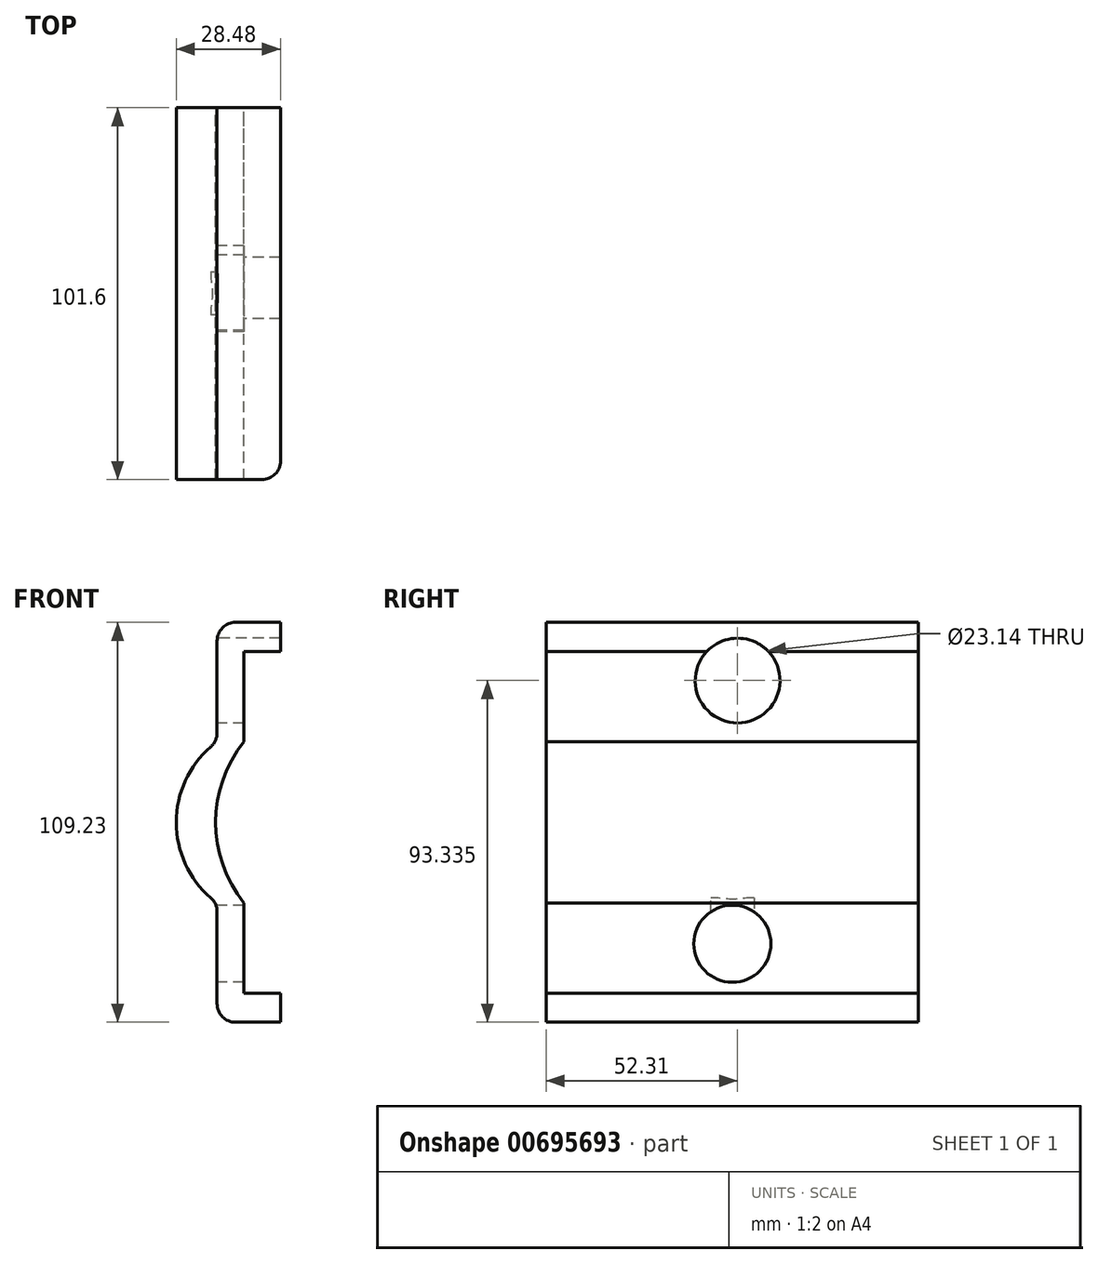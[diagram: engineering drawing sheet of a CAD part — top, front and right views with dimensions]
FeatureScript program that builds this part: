
annotation { "Feature Type Name" : "Feature", "Feature Type Description" : "" }
export const myFeature = defineFeature(function(context is Context, id is Id, definition is map)
    precondition{}
    {
        {
            var Q0;
            Q0=qCreatedBy(makeId("Front.planeOp"),FACE);
            var sketch = newSketch(context, id + "F0", { "sketchPlane" : qUnion([Q0])});
            skLineSegment(sketch, "E0", {"start": v(-11.6, 59.9) * mm, "end": v(-28.92, 59.9) * mm});
            skLineSegment(sketch, "E1", {"start": v(-28.92, 59.9) * mm, "end": v(-28.92, 27.3) * mm});
            skLineSegment(sketch, "E2", {"start": v(-11.6, 59.9) * mm, "end": v(-11.6, 51.97) * mm});
            skLineSegment(sketch, "E3", {"start": v(-11.6, 51.97) * mm, "end": v(-21.58, 51.97) * mm});
            skLineSegment(sketch, "E4", {"start": v(-21.58, 51.97) * mm, "end": v(-21.58, 27.3) * mm});
            skLineSegment(sketch, "E5", {"start": v(-28.92, -16.74) * mm, "end": v(-28.92, -49.33) * mm});
            skLineSegment(sketch, "E6", {"start": v(-28.92, -49.33) * mm, "end": v(-11.6, -49.33) * mm});
            skLineSegment(sketch, "E7", {"start": v(-11.6, -49.33) * mm, "end": v(-11.6, -41.4) * mm});
            skLineSegment(sketch, "E8", {"start": v(-11.6, -41.4) * mm, "end": v(-21.58, -41.4) * mm});
            skLineSegment(sketch, "E9", {"start": v(-21.58, -41.4) * mm, "end": v(-21.58, -16.74) * mm});
            skArc(sketch, "E10", {"start": v(-28.92, 27.3) * mm, "mid": v(-40.08, 5.29) * mm, "end": v(-28.92, -16.74) * mm});
            skArc(sketch, "E11", {"start": v(-21.58, 27.3) * mm, "mid": v(-29.3, 5.29) * mm, "end": v(-21.58, -16.74) * mm});
            skSolve(sketch);
        }
        {
            var Q0;
            Q0 = qSketchRegion(id + "F0", true);
            extrude(context, id + "F1", {"entities" : qUnion([Q0]), "depth" : 101.6 * mm, "offsetDistance" : 25.4 * mm});
        }
        {
            var Q0;
            Q0=makeQuery(id+"F1.opExtrude","SWEPT_FACE",FACE,{"disambiguationData":[OSD([sQuery(id+"F0.wireOp",EDGE,"E1")])]});
            var sketch = newSketch(context, id + "F2", { "sketchPlane" : qUnion([Q0])});
            skCircle(sketch, "E12", {"center": v(49.3, 44) * mm, "radius": 11.57 * mm});
            skSolve(sketch);
        }
        {
            var Q0;
            Q0 = qSketchRegion(id + "F2", true);
            extrude(context, id + "F3", {"entities" : qUnion([Q0]), "operationType" : NewBodyOperationType.REMOVE, "oppositeDirection" : true, "depth" : 25.4 * mm, "offsetDistance" : 25.4 * mm});
        }
        {
            var Q0;
            Q0=makeQuery(id+"F1.opExtrude","SWEPT_FACE",FACE,{"disambiguationData":[OSD([sQuery(id+"F0.wireOp",EDGE,"E5")])]});
            var sketch = newSketch(context, id + "F4", { "sketchPlane" : qUnion([Q0])});
            skCircle(sketch, "E13", {"center": v(50.72, -27.9) * mm, "radius": 10.53 * mm});
            skSolve(sketch);
        }
        {
            var Q0;
            Q0 = qSketchRegion(id + "F4", true);
            extrude(context, id + "F5", {"entities" : qUnion([Q0]), "operationType" : NewBodyOperationType.REMOVE, "oppositeDirection" : true, "depth" : 25.4 * mm, "offsetDistance" : 25.4 * mm});
        }
        {
            var Q0;
            Q0=makeQuery(id+"F1.opExtrude","CAP_EDGE",EDGE,{"disambiguationData":[OSD([sQuery(id+"F0.wireOp",EDGE,"E2")])],"isStart":false});
            var Q1;
            Q1=makeQuery(id+"F1.opExtrude","CAP_EDGE",EDGE,{"disambiguationData":[OSD([sQuery(id+"F0.wireOp",EDGE,"E7")])],"isStart":false});
            var Q2;
            Q2=makeQuery(id+"F1.opExtrude","SWEPT_EDGE",EDGE,{"disambiguationData":[OSD([sQuery(id+"F0.wireOp",EDGE,"E5"),sQuery(id+"F0.wireOp",EDGE,"E10")])]});
            var Q3;
            Q3=makeQuery(id+"F1.opExtrude","SWEPT_EDGE",EDGE,{"disambiguationData":[OSD([sQuery(id+"F0.wireOp",EDGE,"E1"),sQuery(id+"F0.wireOp",EDGE,"E10")])]});
            fillet(context, id + "F6", {"entities" : qUnion([Q0, Q1, Q2, Q3]), "radius" : 5.08 * mm, "tangentPropagation" : true, "allowEdgeOverflow" : false});
        }
        {
            var Q0;
            Q0=makeQuery(id+"F1.opExtrude","SWEPT_EDGE",EDGE,{"disambiguationData":[OSD([sQuery(id+"F0.wireOp",EDGE,"E5"),sQuery(id+"F0.wireOp",EDGE,"E6")])]});
            var Q1;
            Q1=makeQuery(id+"F1.opExtrude","SWEPT_EDGE",EDGE,{"disambiguationData":[OSD([sQuery(id+"F0.wireOp",EDGE,"E0"),sQuery(id+"F0.wireOp",EDGE,"E1")])]});
            fillet(context, id + "F7", {"entities" : qUnion([Q0, Q1]), "radius" : 5.08 * mm, "tangentPropagation" : true, "allowEdgeOverflow" : false});
        }
    });
